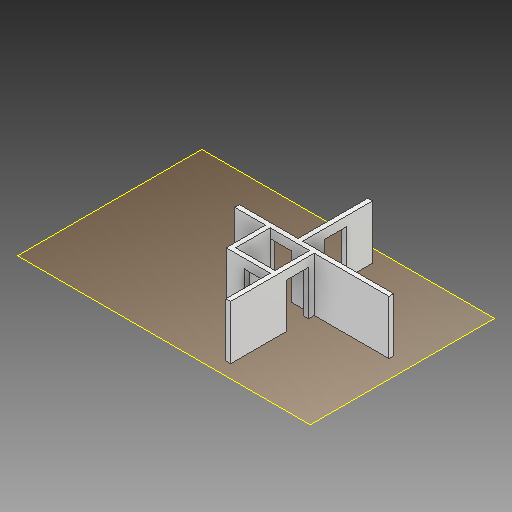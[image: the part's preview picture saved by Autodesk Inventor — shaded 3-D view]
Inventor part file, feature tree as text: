
AUTODESK INVENTOR PART (.ipt)
format: ipt  version: 2017 (Build 210142000, 142)  size: 176,640 bytes
history: native  units: mm
features: extrude x5, sketch x5, projected_geometry x4, other x3, plane x1, reference x1
ambient origin geometry x8: Origin, YZ Plane, XZ Plane, XY Plane, X Axis, Y Axis, Z Axis, Center Point
bodies: Body1 (feature_tree)
feature tree (19):
  plane  "Arbeitsebene1"
  extrude  "Extrusion4"  Depth=200.0mm
  extrude  "Extrusion5"  Depth=200.0mm
  extrude  "Extrusion6"  Depth=200.0mm
  extrude  "Extrusion7"  Depth=2500.0mm
  extrude  "Extrusion8"  Depth=200.0mm
  sketch  "Skizze1"  dims[d0=200.0mm d1=200.0mm]
  reference  "Referenz1"
  sketch  "Skizze4"  dims[d2=200.0mm d3=200.0mm]
  projected_geometry  "Projizierte Kontur3"
  sketch  "Skizze5"  dims[d4=2980.0mm d5=200.0mm d6=200.0mm]
  projected_geometry  "Projizierte Kontur4"
  sketch  "Skizze6"  dims[d8=200.0mm d9=2500.0mm]
  projected_geometry  "Projizierte Kontur5"
  sketch  "Skizze7"  dims[d16=3880.0mm d26=200.0mm d27=200.0mm d28=1310.0mm d29=200.0mm d30=1500.0mm d31=1680.0mm d32=2300.0mm d33=0.0mm d34=950.0mm d35=1900.0mm d36=2300.0mm d37=0.0mm d38=950.0mm d39=1900.0mm d40=2300.0mm d41=0.0mm d42=950.0mm d43=1900.0mm d44=2300.0mm d45=0.0mm d46=950.0mm d47=1900.0mm d48=2300.0mm d49=0.0mm]
  projected_geometry  "Projizierte Kontur6"
  other  "<userpath>\Documents\Inventor\Oli_Grundstück\Haus.iam"
  other  "Haus.iam"
  other  "Zwischendecke:1"
